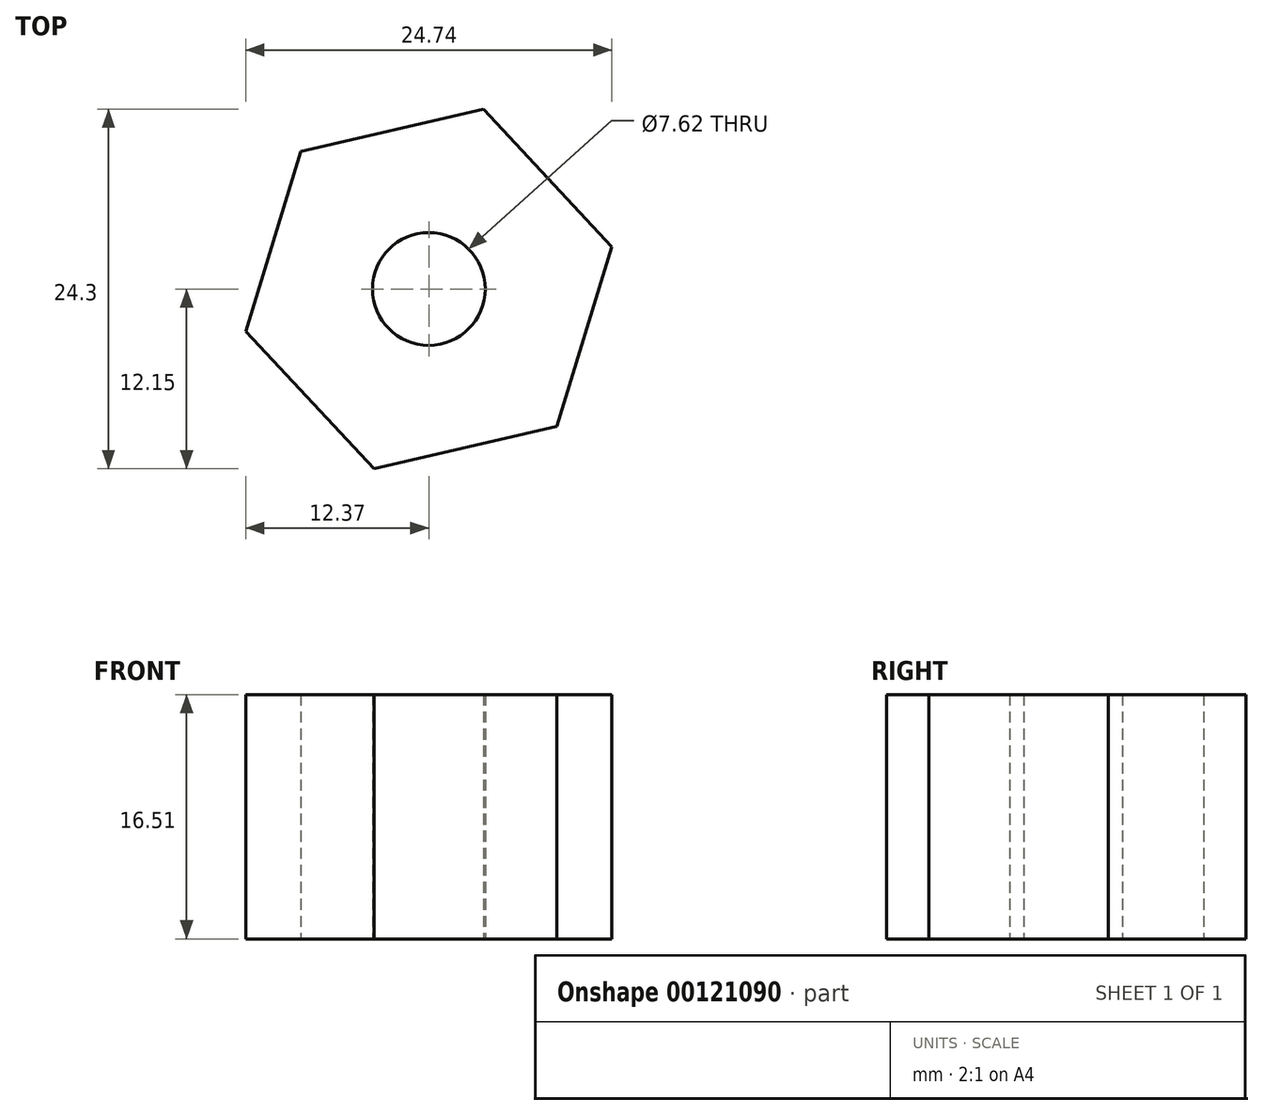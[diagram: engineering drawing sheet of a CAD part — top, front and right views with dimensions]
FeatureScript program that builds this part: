
annotation { "Feature Type Name" : "Feature", "Feature Type Description" : "" }
export const myFeature = defineFeature(function(context is Context, id is Id, definition is map)
    precondition{}
    {
        {
            var Q0;
            Q0=qCreatedBy(makeId("Top.planeOp"),FACE);
            var sketch = newSketch(context, id + "F0", { "sketchPlane" : qUnion([Q0])});
            skCircle(sketch, "E0.cCircle", {"center": v(0, 0) * mm, "radius": 12.7 * mm, "construction": true});
            skLineSegment(sketch, "E0.0", {"start": v(3.71, 12.15) * mm, "end": v(12.37, 2.86) * mm});
            skLineSegment(sketch, "E0.1", {"start": v(12.37, 2.86) * mm, "end": v(8.66, -9.29) * mm});
            skLineSegment(sketch, "E0.2", {"start": v(8.66, -9.29) * mm, "end": v(-3.71, -12.15) * mm});
            skLineSegment(sketch, "E0.3", {"start": v(-3.71, -12.15) * mm, "end": v(-12.37, -2.86) * mm});
            skLineSegment(sketch, "E0.4", {"start": v(-12.37, -2.86) * mm, "end": v(-8.66, 9.29) * mm});
            skLineSegment(sketch, "E0.5", {"start": v(-8.66, 9.29) * mm, "end": v(3.71, 12.15) * mm});
            skCircle(sketch, "E1", {"center": v(0, 0) * mm, "radius": 3.8 * mm});
            skSolve(sketch);
        }
        {
            var Q0;
            Q0=makeQuery(id+"F0.imprint","IMPRINT",FACE,{"disambiguationData":[TD([[makeQuery(id+"F0.imprint","IMPRINT",EDGE,{"derivedFrom":sQuery(id+"F0.wireOp",EDGE,"E0.0")}),-1.0]])]});
            extrude(context, id + "F1", {"entities" : qUnion([Q0]), "depth" : 16.5 * mm});
        }
    });
